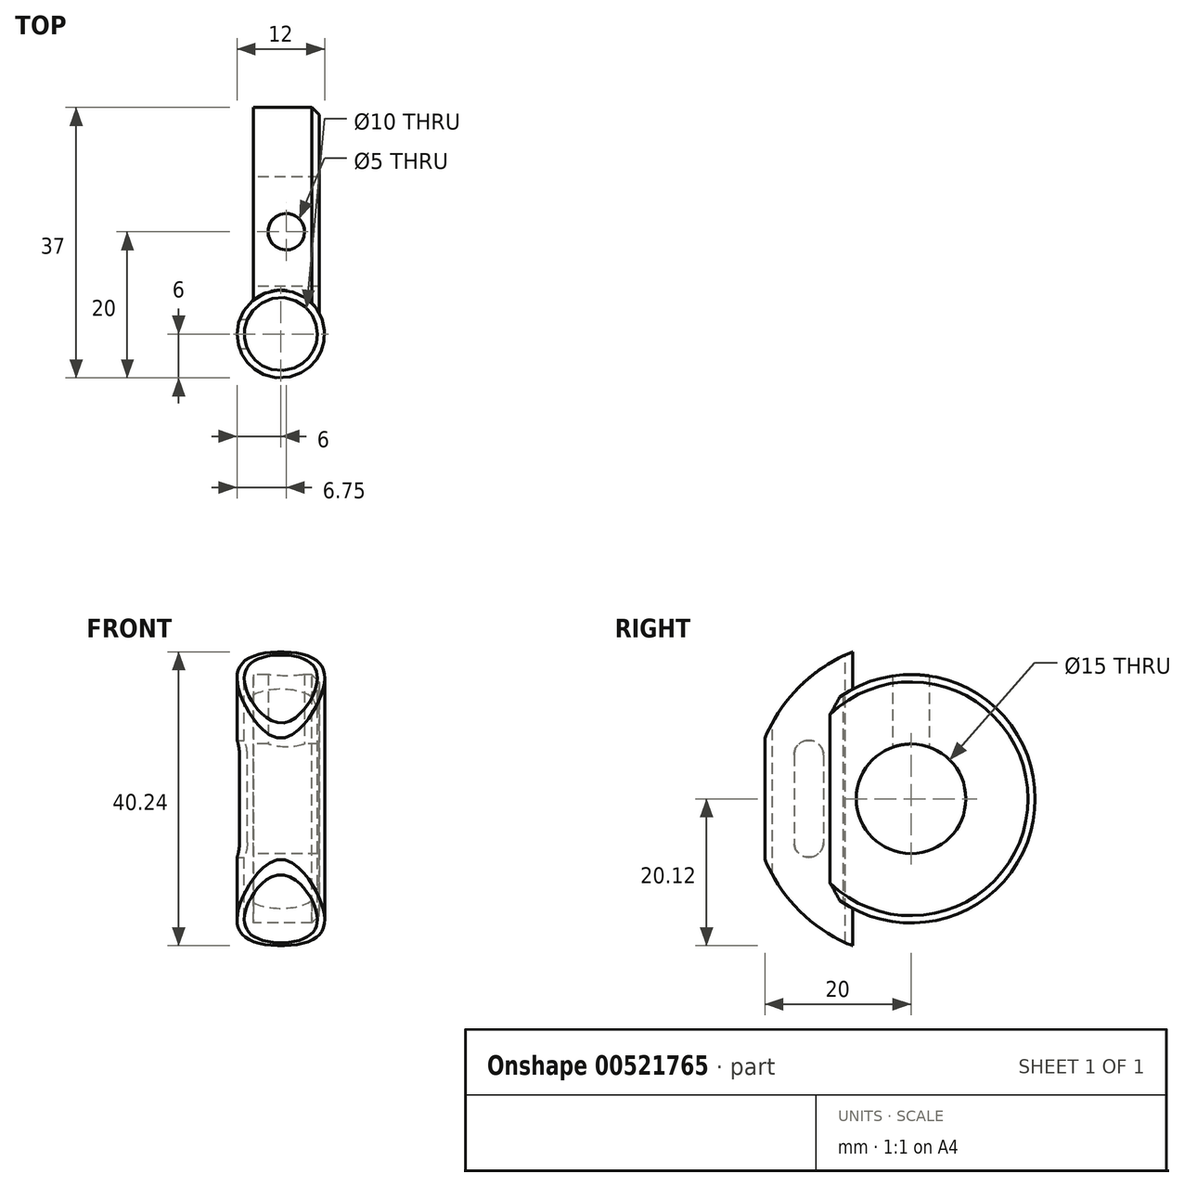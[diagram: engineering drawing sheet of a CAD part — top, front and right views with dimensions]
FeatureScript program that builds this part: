
annotation { "Feature Type Name" : "Feature", "Feature Type Description" : "" }
export const myFeature = defineFeature(function(context is Context, id is Id, definition is map)
    precondition{}
    {
        {
            var Q0;
            Q0=qCreatedBy(makeId("Right.planeOp"),FACE);
            var sketch = newSketch(context, id + "F0", { "sketchPlane" : qUnion([Q0])});
            skCircle(sketch, "E0", {"center": v(0, 0) * mm, "radius": 7.5 * mm});
            skCircle(sketch, "E1", {"center": v(0, 0) * mm, "radius": 17 * mm});
            skSolve(sketch);
        }
        {
            var Q0;
            Q0=makeQuery(id+"F0.imprint","IMPRINT",FACE,{"disambiguationData":[TD([[makeQuery(id+"F0.imprint","IMPRINT",EDGE,{"derivedFrom":sQuery(id+"F0.wireOp",EDGE,"E0")}),-1.0]])]});
            extrude(context, id + "F1", {"entities" : qUnion([Q0]), "depth" : 9 * mm, "offsetDistance" : 25 * mm});
        }
        {
            var Q0;
            Q0=qCreatedBy(makeId("Top.planeOp"),FACE);
            var sketch = newSketch(context, id + "F2", { "sketchPlane" : qUnion([Q0])});
            skCircle(sketch, "E2", {"center": v(4.5, 0) * mm, "radius": 2.5 * mm});
            skSolve(sketch);
        }
        {
            var Q0;
            Q0=makeQuery(id+"F6.boolean.opBoolean","SPLIT",EDGE,{"disambiguationData":[OD(1.0)],"derivedFrom":makeQuery(id+"F1.opExtrude","CAP_EDGE",EDGE,{"disambiguationData":[OSD([sQuery(id+"F0.wireOp",EDGE,"E1")])],"isStart":false})});
            chamfer(context, id + "F3", {"entities" : qUnion([Q0]), "width" : 1 * mm, "tangentPropagation" : true});
        }
        {
            var Q0;
            Q0 = qSketchRegion(id + "F2", true);
            extrude(context, id + "F4", {"entities" : qUnion([Q0]), "operationType" : NewBodyOperationType.REMOVE, "depth" : 25 * mm, "offsetDistance" : 25 * mm});
        }
        {
            var Q0;
            Q0=qCreatedBy(makeId("Top.planeOp"),FACE);
            var sketch = newSketch(context, id + "F5", { "sketchPlane" : qUnion([Q0])});
            skCircle(sketch, "E3", {"center": v(3.75, -14) * mm, "radius": 6 * mm});
            skLineSegment(sketch, "E4", {"start": v(-29.2, -23.15) * mm, "end": v(16.03, -23.15) * mm, "construction": true});
            skSolve(sketch);
        }
        {
            var Q0;
            Q0=makeQuery(id+"F5.imprint","IMPRINT",FACE,{"disambiguationData":[TD([[makeQuery(id+"F5.imprint","IMPRINT",EDGE,{"derivedFrom":sQuery(id+"F5.wireOp",EDGE,"E3")}),1.0]])]});
            extrude(context, id + "F6", {"entities" : qUnion([Q0]), "operationType" : NewBodyOperationType.ADD, "depth" : 25 * mm, "offsetDistance" : 25 * mm, "hasSecondDirection" : true, "secondDirectionOppositeDirection" : true, "secondDirectionDepth" : 25 * mm});
        }
        {
            var Q0;
            Q0=qCreatedBy(makeId("Right.planeOp"),FACE);
            var sketch = newSketch(context, id + "F7", { "sketchPlane" : qUnion([Q0])});
            skCircle(sketch, "E5", {"center": v(0, 0) * mm, "radius": 21.65 * mm});
            skCircle(sketch, "E6", {"center": v(0, 0) * mm, "radius": 36.98 * mm});
            skSolve(sketch);
        }
        {
            var Q0;
            Q0=makeQuery(id+"F7.imprint","IMPRINT",FACE,{"disambiguationData":[TD([[makeQuery(id+"F7.imprint","IMPRINT",EDGE,{"derivedFrom":sQuery(id+"F7.wireOp",EDGE,"E5")}),-1.0]])]});
            extrude(context, id + "F8", {"entities" : qUnion([Q0]), "operationType" : NewBodyOperationType.REMOVE, "depth" : 25 * mm, "offsetDistance" : 25 * mm, "hasSecondDirection" : true, "secondDirectionOppositeDirection" : true, "secondDirectionDepth" : 25 * mm});
        }
        {
            var Q0;
            Q0=qCreatedBy(makeId("Top.planeOp"),FACE);
            var sketch = newSketch(context, id + "F9", { "sketchPlane" : qUnion([Q0])});
            skCircle(sketch, "E7", {"center": v(3.75, -14) * mm, "radius": 5 * mm});
            skSolve(sketch);
        }
        {
            var Q0;
            Q0 = qSketchRegion(id + "F9", true);
            extrude(context, id + "F10", {"entities" : qUnion([Q0]), "operationType" : NewBodyOperationType.REMOVE, "oppositeDirection" : true, "depth" : 25 * mm, "offsetDistance" : 25 * mm, "hasSecondDirection" : true, "secondDirectionOppositeDirection" : false, "secondDirectionDepth" : 25 * mm});
        }
        {
            var Q0;
            Q0=qCreatedBy(makeId("Right.planeOp"),FACE);
            var sketch = newSketch(context, id + "F11", { "sketchPlane" : qUnion([Q0])});
            skLineSegment(sketch, "E8.left", {"start": v(-12, 6) * mm, "end": v(-12, -6) * mm});
            skLineSegment(sketch, "E8.right", {"start": v(-16, 6) * mm, "end": v(-16, -6) * mm});
            skArc(sketch, "E9", {"start": v(-12, 6) * mm, "mid": v(-14, 8) * mm, "end": v(-16, 6) * mm});
            skArc(sketch, "E10", {"start": v(-16, -6) * mm, "mid": v(-14, -8) * mm, "end": v(-12, -6) * mm});
            skSolve(sketch);
        }
        {
            var Q0;
            Q0 = qSketchRegion(id + "F11", true);
            extrude(context, id + "F12", {"entities" : qUnion([Q0]), "operationType" : NewBodyOperationType.REMOVE, "oppositeDirection" : true, "depth" : 25 * mm, "offsetDistance" : 25 * mm});
        }
    });
